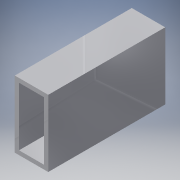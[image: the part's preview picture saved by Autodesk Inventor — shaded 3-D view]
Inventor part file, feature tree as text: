
AUTODESK INVENTOR PART (.ipt)
format: ipt  version: 2016 (Build 200138000, 138)  size: 95,744 bytes
history: native  units: in
note: dims shown in document units (in); Inventor stores cm internally (conversion verified against a paired STEP export)
features: extrude x1, sketch x1
ambient origin geometry x8: Origin, YZ Plane, XZ Plane, XY Plane, X Axis, Y Axis, Z Axis, Center Point
bodies: Solid1 (feature_tree)
feature tree (2):
  extrude  "Extrusion1"  Depth=2.0in
  sketch  "Sketch1"  dims[d0=1.0in d1=2.0in d2=0.125in d3=0.125in d4=0.125in d5=0.125in d6=3.5in d7=0.0in]
